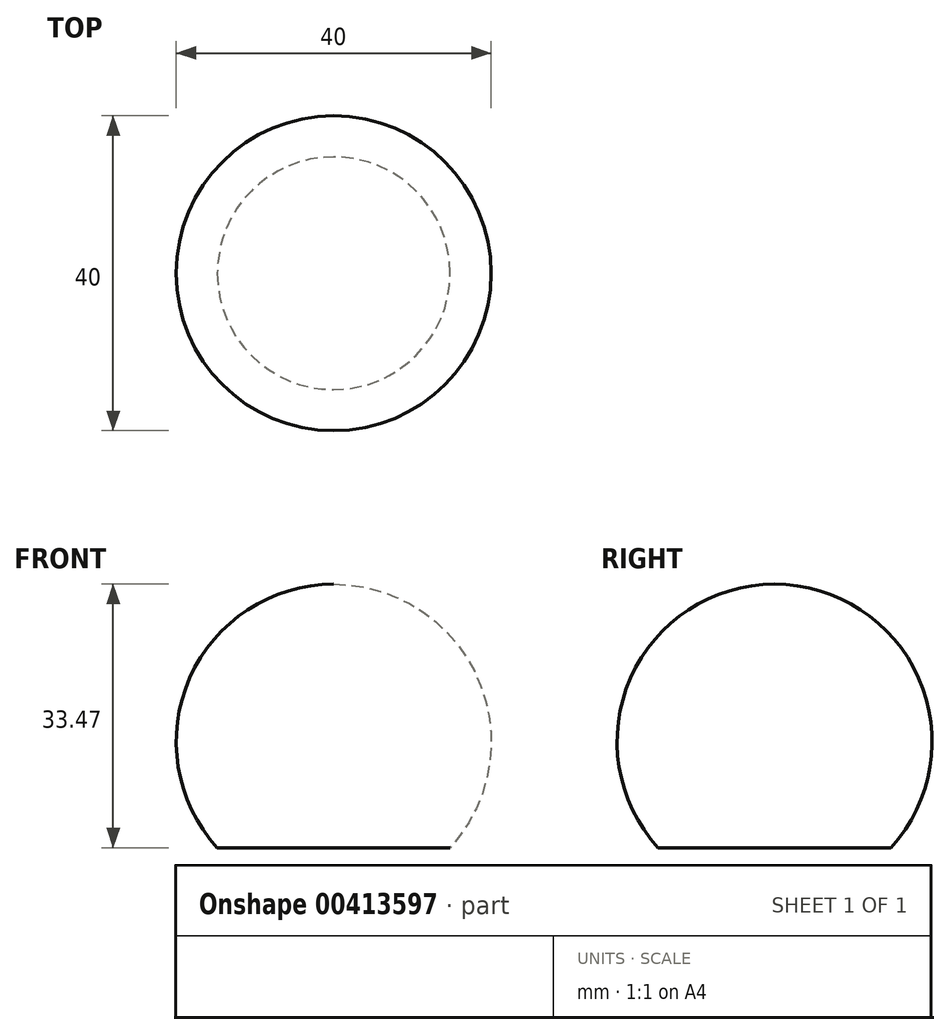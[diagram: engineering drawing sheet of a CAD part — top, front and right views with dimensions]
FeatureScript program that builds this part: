
annotation { "Feature Type Name" : "Feature", "Feature Type Description" : "" }
export const myFeature = defineFeature(function(context is Context, id is Id, definition is map)
    precondition{}
    {
        {
            var Q0;
            Q0=qCreatedBy(makeId("Front.planeOp"),FACE);
            var sketch = newSketch(context, id + "F0", { "sketchPlane" : qUnion([Q0])});
            skArc(sketch, "E0", {"start": v(0, 20) * mm, "mid": v(-18.3, 8.08) * mm, "end": v(-14.78, -13.47) * mm});
            skLineSegment(sketch, "E1", {"start": v(-14.78, -13.47) * mm, "end": v(0, -13.47) * mm});
            skLineSegment(sketch, "E2", {"start": v(0, -13.47) * mm, "end": v(0, 20) * mm});
            skSolve(sketch);
        }
        {
            var Q0;
            Q0 = qSketchRegion(id + "F0", true);
            var Q1;
            Q1=sQuery(id+"F0.wireOp",EDGE,"E2");
            revolve(context, id + "F1", {"entities" : qUnion([Q0]), "axis" : qUnion([Q1]), "revolveType" : RevolveType.FULL});
        }
    });
